# Revit family: Cleanouts-Drain-Floor-WATTS-RD-CO12-SQ
name_source: partatom
category: Plumbing Fixtures
units: mm (PartAtom-declared; Revit-internal decimal feet)

## family parameters
Cut with Voids When Loaded = No
Host = Face
OmniClass Number = 23.70.50.21.24.11
OmniClass Title = Roof Waste Water Drains
Part Type = Normal
Room Calculation Point = No
Round Connector Dimension = Use Radius
Shared = No

## types (6) — shared parameters
-SS Stainless Steel = No
ADA Compliant = Yes
Assembly Code = D2040200
Body Length = 2"
Body Radius = 2 1/2"
CW Connection = No
Country = United States
Default Elevation = 0"
Description = PVC/ABS Adjustable Floor Cleanout w/Square Top
Finish = Plastic-WATTS- PVC-White
Flange Collar Radius = 2 13/16"
Flange Radius = 3 3/16"
Flange Thickness = 5/16"
Grate Width = 5 1/8"
HW Connection = No
Manufacturer = WATTS
Manufacturer Product Line = Drainage Products
Model = CO12-SQ
Outlet Length = 2"
Product Documentation Link = https://www.watts.com
Product Page URL = https://www.watts.com
Region = North America
URL = http://www.watts.com
Vent Connection = No
Waste Connection = Yes
zero-valued in all types: CWFU, HWFU, WFU

## per-type parameters (varying)
| type | -DI Ductile Iron Top | -VP Vandal Proof Screws | Connection Description | Connection Size | Grate Dimension | Grate Height | Material | Outlet Radius |
| 4" Pipe Size - ABS-WATTS-002 | No | Yes | 4" ABS Connection Outlet | 4" | 7/8" | 7/8" | Plastic-WATTS-ABS-002 | 2" |
| 3" Pipe Size -ABS-WATTS-002 | Yes | No | 3" ABS Connection Outlet | 3" | 2 3/4" | 9" | Plastic-WATTS-ABS-002 | 1 1/2" |
| 2" Pipe Size - ABS-WATTS-002 | Yes | No | 2" ABS Connection Outlet | 2" | 1" | 1" | Plastic-WATTS-ABS-002 | 1" |
| 2" Pipe Size - PVC-WATTS-002 | No | Yes | 2" PVC Connection Outlet | 2" | 1" | 1" | Plastic-WATTS-PVC-002 | 1" |
| 3" Pipe Size - PVC-WATTS-002 | No | No | 3" PVC Connection Outlet | 3" | 2 3/4" | 2 3/4" | Plastic-WATTS-PVC-002 | 1 1/2" |
| 4" Pipe Size - PVC-WATTS-002 | Yes | No | 4" PVC Connection Outlet | 4" | 7/8" | 7/8" | Plastic-WATTS-PVC-002 | 2" |

## geometry (parser evidence)
native form markers: Sweep x2
no freeform markers — native parametric forms only
